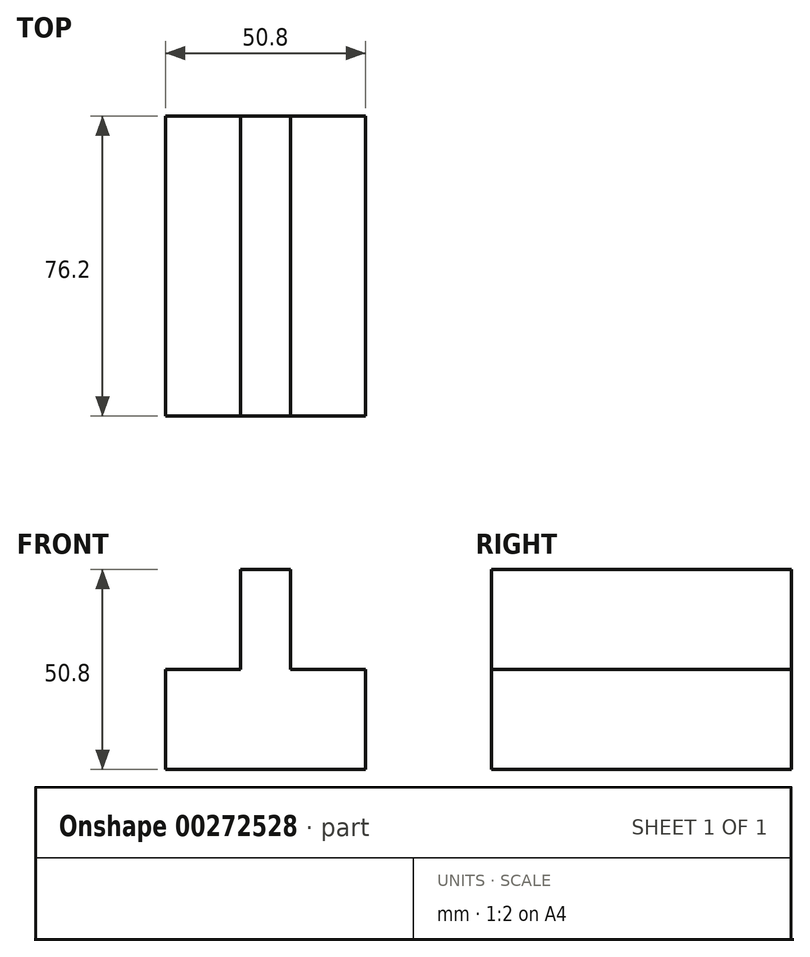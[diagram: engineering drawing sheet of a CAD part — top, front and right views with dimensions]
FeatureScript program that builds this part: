
annotation { "Feature Type Name" : "Feature", "Feature Type Description" : "" }
export const myFeature = defineFeature(function(context is Context, id is Id, definition is map)
    precondition{}
    {
        {
            var Q0;
            Q0=qCreatedBy(makeId("Front.planeOp"),FACE);
            var sketch = newSketch(context, id + "F0", { "sketchPlane" : qUnion([Q0])});
            skLineSegment(sketch, "E0", {"start": v(0, 0) * mm, "end": v(-50.8, 0) * mm});
            skLineSegment(sketch, "E1", {"start": v(-50.8, 0) * mm, "end": v(-50.8, 25.4) * mm});
            skLineSegment(sketch, "E2", {"start": v(-50.8, 25.4) * mm, "end": v(-31.75, 25.4) * mm});
            skLineSegment(sketch, "E3", {"start": v(-31.75, 25.4) * mm, "end": v(-31.75, 50.8) * mm});
            skLineSegment(sketch, "E4", {"start": v(-31.75, 50.8) * mm, "end": v(-19.05, 50.8) * mm});
            skLineSegment(sketch, "E5", {"start": v(-19.05, 50.8) * mm, "end": v(-19.05, 25.4) * mm});
            skLineSegment(sketch, "E6", {"start": v(-19.05, 25.4) * mm, "end": v(0, 25.4) * mm});
            skLineSegment(sketch, "E7", {"start": v(0, 25.4) * mm, "end": v(0, 0) * mm});
            skSolve(sketch);
        }
        {
            var Q0;
            Q0 = qSketchRegion(id + "F0", true);
            extrude(context, id + "F1", {"entities" : qUnion([Q0]), "depth" : 76.2 * mm});
        }
    });
